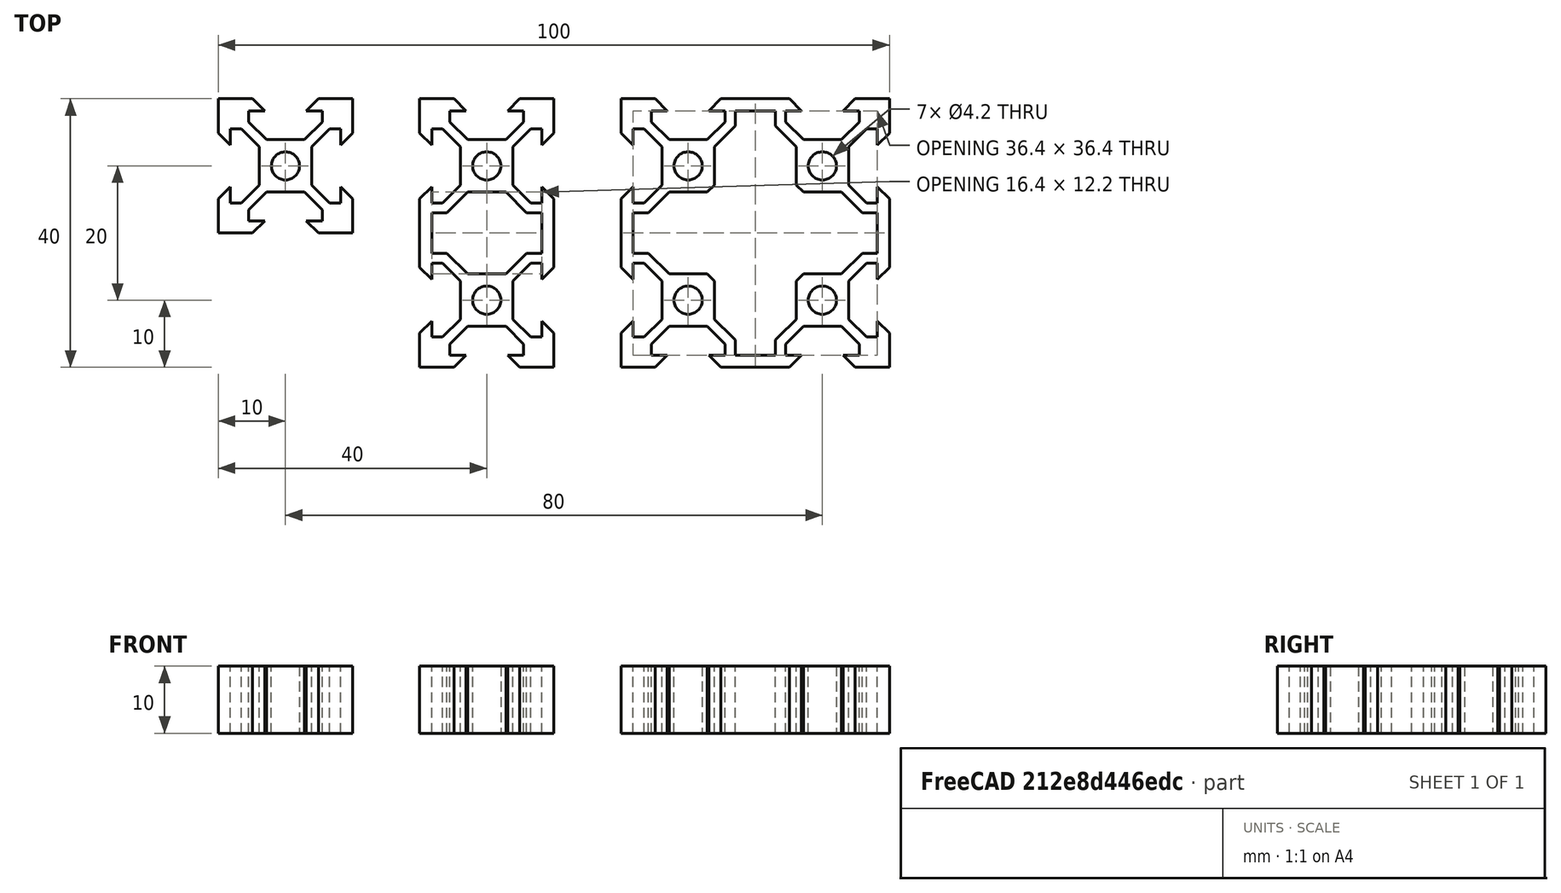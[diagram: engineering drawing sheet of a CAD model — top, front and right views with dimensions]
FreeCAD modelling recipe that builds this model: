
FCSTD DOCUMENT  (FreeCAD 0.19R24291 (Git))
Label: v slot
License: Free for Commercial Use
objects: Sketcher::SketchObject×3, Part::Extrusion×3
note: 6 computed .brp shape members not serialized (recipe doc carries the construction recipe); baked Part::Feature solids carry a one-line shape summary decoded from their .brp

FEATURE [Sketcher::SketchObject] Sketch
  FullyConstrained = false
  sketch-geometry (49):
    g0: Circle CenterX=0 CenterY=0 CenterZ=0 NormalX=0 NormalY=0 NormalZ=-1 AngleXU=0 Radius=2.1
    g1: LineSegment StartX=-2.84 StartY=3.90066 StartZ=0 EndX=-5.49934 EndY=6.56 EndZ=0
    g2: LineSegment StartX=-5.49934 StartY=6.56 StartZ=0 EndX=-5.49934 EndY=8.2 EndZ=0
    g3: LineSegment StartX=-5.49934 StartY=8.2 StartZ=0 EndX=-3.1 EndY=8.2 EndZ=0
    g4: LineSegment StartX=-3.1 StartY=8.2 StartZ=0 EndX=-4.9 EndY=10 EndZ=0
    g5: LineSegment StartX=-4.9 StartY=10 StartZ=0 EndX=-10 EndY=10 EndZ=0
    g6: LineSegment StartX=-10 StartY=10 StartZ=0 EndX=-10 EndY=4.9 EndZ=0
    g7: LineSegment StartX=-10 StartY=4.9 StartZ=0 EndX=-8.2 EndY=3.1 EndZ=0
    g8: LineSegment StartX=-8.2 StartY=3.1 StartZ=0 EndX=-8.2 EndY=5.49934 EndZ=0
    g9: LineSegment StartX=-8.2 StartY=5.49934 StartZ=0 EndX=-6.56 EndY=5.49934 EndZ=0
    g10: LineSegment StartX=-6.56 StartY=5.49934 StartZ=0 EndX=-3.90066 EndY=2.84 EndZ=0
    g11: LineSegment StartX=-3.90066 StartY=2.84 StartZ=0 EndX=-3.90066 EndY=-1.3e-15 EndZ=0
    g12: LineSegment StartX=-3.90066 StartY=-1.1e-15 StartZ=0 EndX=-3.90066 EndY=-2.84 EndZ=0
    g13: LineSegment StartX=-3.90066 StartY=-2.84 StartZ=0 EndX=-6.56 EndY=-5.49934 EndZ=0
    g14: LineSegment StartX=-6.56 StartY=-5.49934 StartZ=0 EndX=-8.2 EndY=-5.49934 EndZ=0
    g15: LineSegment StartX=-8.2 StartY=-5.49934 StartZ=0 EndX=-8.2 EndY=-3.1 EndZ=0
    g16: LineSegment StartX=-8.2 StartY=-3.1 StartZ=0 EndX=-10 EndY=-4.9 EndZ=0
    g17: LineSegment StartX=-10 StartY=-4.9 StartZ=0 EndX=-10 EndY=-10 EndZ=0
    g18: LineSegment StartX=-10 StartY=-10 StartZ=0 EndX=-4.9 EndY=-10 EndZ=0
    g19: LineSegment StartX=-4.9 StartY=-10 StartZ=0 EndX=-3.1 EndY=-8.2 EndZ=0
    g20: LineSegment StartX=-3.1 StartY=-8.2 StartZ=0 EndX=-5.49934 EndY=-8.2 EndZ=0
    g21: LineSegment StartX=-5.49934 StartY=-8.2 StartZ=0 EndX=-5.49934 EndY=-6.56 EndZ=0
    g22: LineSegment StartX=-5.49934 StartY=-6.56 StartZ=0 EndX=-2.84 EndY=-3.90066 EndZ=0
    g23: LineSegment StartX=-2.84 StartY=-3.90066 StartZ=0 EndX=-4e-16 EndY=-3.90066 EndZ=0
    g24: LineSegment StartX=-6e-16 StartY=-3.90066 StartZ=0 EndX=2.84 EndY=-3.90066 EndZ=0
    g25: LineSegment StartX=2.84 StartY=-3.90066 StartZ=0 EndX=5.49934 EndY=-6.56 EndZ=0
    g26: LineSegment StartX=5.49934 StartY=-6.56 StartZ=0 EndX=5.49934 EndY=-8.2 EndZ=0
    g27: LineSegment StartX=5.49934 StartY=-8.2 StartZ=0 EndX=3.1 EndY=-8.2 EndZ=0
    g28: LineSegment StartX=3.1 StartY=-8.2 StartZ=0 EndX=4.9 EndY=-10 EndZ=0
    g29: LineSegment StartX=4.9 StartY=-10 StartZ=0 EndX=10 EndY=-10 EndZ=0
    g30: LineSegment StartX=10 StartY=-10 StartZ=0 EndX=10 EndY=-4.9 EndZ=0
    g31: LineSegment StartX=10 StartY=-4.9 StartZ=0 EndX=8.2 EndY=-3.1 EndZ=0
    g32: LineSegment StartX=8.2 StartY=-3.1 StartZ=0 EndX=8.2 EndY=-5.49934 EndZ=0
    g33: LineSegment StartX=8.2 StartY=-5.49934 StartZ=0 EndX=6.56 EndY=-5.49934 EndZ=0
    g34: LineSegment StartX=6.56 StartY=-5.49934 StartZ=0 EndX=3.90066 EndY=-2.84 EndZ=0
    g35: LineSegment StartX=3.90066 StartY=-2.84 StartZ=0 EndX=3.90066 EndY=-1.3e-15 EndZ=0
    g36: LineSegment StartX=3.90066 StartY=-1.1e-15 StartZ=0 EndX=3.90066 EndY=2.84 EndZ=0
    g37: LineSegment StartX=3.90066 StartY=2.84 StartZ=0 EndX=6.56 EndY=5.49934 EndZ=0
    g38: LineSegment StartX=6.56 StartY=5.49934 StartZ=0 EndX=8.2 EndY=5.49934 EndZ=0
    g39: LineSegment StartX=8.2 StartY=5.49934 StartZ=0 EndX=8.2 EndY=3.1 EndZ=0
    g40: LineSegment StartX=8.2 StartY=3.1 StartZ=0 EndX=10 EndY=4.9 EndZ=0
    g41: LineSegment StartX=10 StartY=4.9 StartZ=0 EndX=10 EndY=10 EndZ=0
    g42: LineSegment StartX=10 StartY=10 StartZ=0 EndX=4.9 EndY=10 EndZ=0
    g43: LineSegment StartX=4.9 StartY=10 StartZ=0 EndX=3.1 EndY=8.2 EndZ=0
    g44: LineSegment StartX=3.1 StartY=8.2 StartZ=0 EndX=5.49934 EndY=8.2 EndZ=0
    g45: LineSegment StartX=5.49934 StartY=8.2 StartZ=0 EndX=5.49934 EndY=6.56 EndZ=0
    g46: LineSegment StartX=5.49934 StartY=6.56 StartZ=0 EndX=2.84 EndY=3.90066 EndZ=0
    g47: LineSegment StartX=2.84 StartY=3.90066 StartZ=0 EndX=0 EndY=3.90066 EndZ=0
    g48: LineSegment StartX=0 StartY=3.90066 StartZ=0 EndX=-2.84 EndY=3.90066 EndZ=0
FEATURE [Part::Extrusion] Extrude  label="2020"
  Base = -> Sketch
  Dir = (0,0,1)
  DirMode = 2
  FaceMakerClass = Part::FaceMakerBullseye
  LengthFwd = 10
  LengthRev = 0
  Solid = true
  Symmetric = false
FEATURE [Sketcher::SketchObject] Sketch001
  FullyConstrained = false
  sketch-geometry (88):
    g0: LineSegment StartX=35.9387 StartY=-6.99934 StartZ=0 EndX=32.84 EndY=-3.90066 EndZ=0
    g1: LineSegment StartX=32.84 StartY=-3.90066 StartZ=0 EndX=30 EndY=-3.90066 EndZ=0
    g2: LineSegment StartX=30 StartY=-3.90066 StartZ=0 EndX=27.16 EndY=-3.90066 EndZ=0
    g3: LineSegment StartX=27.16 StartY=-3.90066 StartZ=0 EndX=24.0613 EndY=-6.99934 EndZ=0
    g4: LineSegment StartX=24.0613 StartY=-6.99934 StartZ=0 EndX=21.8 EndY=-6.99934 EndZ=0
    g5: LineSegment StartX=21.8 StartY=-6.99934 StartZ=0 EndX=21.8 EndY=-13.0007 EndZ=0
    g6: LineSegment StartX=21.8 StartY=-13.0007 StartZ=0 EndX=24.0613 EndY=-13.0007 EndZ=0
    g7: LineSegment StartX=24.0613 StartY=-13.0007 StartZ=0 EndX=27.16 EndY=-16.0993 EndZ=0
    g8: LineSegment StartX=27.16 StartY=-16.0993 StartZ=0 EndX=30 EndY=-16.0993 EndZ=0
    g9: LineSegment StartX=30 StartY=-16.0993 StartZ=0 EndX=32.84 EndY=-16.0993 EndZ=0
    g10: LineSegment StartX=32.84 StartY=-16.0993 StartZ=0 EndX=35.9387 EndY=-13.0007 EndZ=0
    g11: LineSegment StartX=35.9387 StartY=-13.0007 StartZ=0 EndX=38.2 EndY=-13.0007 EndZ=0
    g12: LineSegment StartX=38.2 StartY=-13.0007 StartZ=0 EndX=38.2 EndY=-6.99934 EndZ=0
    g13: LineSegment StartX=38.2 StartY=-6.99934 StartZ=0 EndX=35.9387 EndY=-6.99934 EndZ=0
    g14: LineSegment StartX=20 StartY=10 StartZ=0 EndX=20 EndY=4.9 EndZ=0
    g15: LineSegment StartX=26.0993 StartY=-9e-16 StartZ=0 EndX=26.0993 EndY=-2.84 EndZ=0
    g16: LineSegment StartX=24.5007 StartY=8.2 StartZ=0 EndX=26.9 EndY=8.2 EndZ=0
    g17: LineSegment StartX=24.5007 StartY=8.2 StartZ=0 EndX=24.5007 EndY=6.56 EndZ=0
    g18: LineSegment StartX=25.1 StartY=10 StartZ=0 EndX=20 EndY=10 EndZ=0
    g19: LineSegment StartX=21.8 StartY=-3.1 StartZ=0 EndX=20 EndY=-4.9 EndZ=0
    g20: LineSegment StartX=38.2 StartY=5.49934 StartZ=0 EndX=36.56 EndY=5.49934 EndZ=0
    g21: LineSegment StartX=38.2 StartY=3.1 StartZ=0 EndX=40 EndY=4.9 EndZ=0
    g22: LineSegment StartX=33.9007 StartY=2.84 StartZ=0 EndX=36.56 EndY=5.49934 EndZ=0
    g23: LineSegment StartX=40 StartY=4.9 StartZ=0 EndX=40 EndY=10 EndZ=0
    g24: LineSegment StartX=26.0993 StartY=-2.84 StartZ=0 EndX=23.44 EndY=-5.49934 EndZ=0
    g25: LineSegment StartX=23.44 StartY=5.49934 StartZ=0 EndX=26.0993 EndY=2.84 EndZ=0
    g26: LineSegment StartX=26.9 StartY=8.2 StartZ=0 EndX=25.1 EndY=10 EndZ=0
    g27: LineSegment StartX=24.5007 StartY=6.56 StartZ=0 EndX=27.16 EndY=3.90066 EndZ=0
    g28: LineSegment StartX=21.8 StartY=3.1 StartZ=0 EndX=21.8 EndY=5.49934 EndZ=0
    g29: LineSegment StartX=33.9007 StartY=-2.84 StartZ=0 EndX=36.56 EndY=-5.49934 EndZ=0
    g30: LineSegment StartX=21.8 StartY=-5.49934 StartZ=0 EndX=23.44 EndY=-5.49934 EndZ=0
    g31: LineSegment StartX=21.8 StartY=5.49934 StartZ=0 EndX=23.44 EndY=5.49934 EndZ=0
    g32: LineSegment StartX=35.4993 StartY=8.2 StartZ=0 EndX=35.4993 EndY=6.56 EndZ=0
    g33: LineSegment StartX=33.1 StartY=8.2 StartZ=0 EndX=35.4993 EndY=8.2 EndZ=0
    g34: LineSegment StartX=38.2 StartY=-3.1 StartZ=0 EndX=38.2 EndY=-5.49934 EndZ=0
    g35: LineSegment StartX=38.2 StartY=-5.49934 StartZ=0 EndX=36.56 EndY=-5.49934 EndZ=0
    g36: LineSegment StartX=26.0993 StartY=-9e-16 StartZ=0 EndX=26.0993 EndY=2.84 EndZ=0
    g37: LineSegment StartX=35.4993 StartY=6.56 StartZ=0 EndX=32.84 EndY=3.90066 EndZ=0
    g38: LineSegment StartX=38.2 StartY=5.49934 StartZ=0 EndX=38.2 EndY=3.1 EndZ=0
    g39: Circle CenterX=30 CenterY=0 CenterZ=0 NormalX=0 NormalY=0 NormalZ=-1 AngleXU=0 Radius=2.1
    g40: LineSegment StartX=30 StartY=3.90066 StartZ=0 EndX=32.84 EndY=3.90066 EndZ=0
    g41: LineSegment StartX=33.9007 StartY=-9e-16 StartZ=0 EndX=33.9007 EndY=2.84 EndZ=0
    g42: LineSegment StartX=21.8 StartY=-5.49934 StartZ=0 EndX=21.8 EndY=-3.1 EndZ=0
    g43: LineSegment StartX=40 StartY=-10 StartZ=0 EndX=40 EndY=-4.9 EndZ=0
    g44: LineSegment StartX=30 StartY=3.90066 StartZ=0 EndX=27.16 EndY=3.90066 EndZ=0
    g45: LineSegment StartX=40 StartY=10 StartZ=0 EndX=34.9 EndY=10 EndZ=0
    g46: LineSegment StartX=33.1 StartY=8.2 StartZ=0 EndX=34.9 EndY=10 EndZ=0
    g47: LineSegment StartX=33.9007 StartY=-9e-16 StartZ=0 EndX=33.9007 EndY=-2.84 EndZ=0
    g48: LineSegment StartX=38.2 StartY=-3.1 StartZ=0 EndX=40 EndY=-4.9 EndZ=0
    g49: LineSegment StartX=21.8 StartY=3.1 StartZ=0 EndX=20 EndY=4.9 EndZ=0
    g50: LineSegment StartX=20 StartY=-4.9 StartZ=0 EndX=20 EndY=-10 EndZ=0
    g51: LineSegment StartX=38.2 StartY=-14.5007 StartZ=0 EndX=38.2 EndY=-16.9 EndZ=0
    g52: LineSegment StartX=38.2 StartY=-23.1 StartZ=0 EndX=38.2 EndY=-25.4993 EndZ=0
    g53: LineSegment StartX=33.9007 StartY=-17.16 StartZ=0 EndX=36.56 EndY=-14.5007 EndZ=0
    g54: LineSegment StartX=32.84 StartY=-23.9007 StartZ=0 EndX=35.4993 EndY=-26.56 EndZ=0
    g55: LineSegment StartX=38.2 StartY=-25.4993 StartZ=0 EndX=36.56 EndY=-25.4993 EndZ=0
    g56: LineSegment StartX=33.9007 StartY=-22.84 StartZ=0 EndX=36.56 EndY=-25.4993 EndZ=0
    g57: LineSegment StartX=38.2 StartY=-14.5007 StartZ=0 EndX=36.56 EndY=-14.5007 EndZ=0
    g58: LineSegment StartX=35.4993 StartY=-28.2 StartZ=0 EndX=35.4993 EndY=-26.56 EndZ=0
    g59: LineSegment StartX=34.9 StartY=-30 StartZ=0 EndX=40 EndY=-30 EndZ=0
    g60: LineSegment StartX=33.9007 StartY=-20 StartZ=0 EndX=33.9007 EndY=-17.16 EndZ=0
    g61: LineSegment StartX=38.2 StartY=-16.9 StartZ=0 EndX=40 EndY=-15.1 EndZ=0
    g62: LineSegment StartX=24.5007 StartY=-26.56 StartZ=0 EndX=27.16 EndY=-23.9007 EndZ=0
    g63: LineSegment StartX=21.8 StartY=-14.5007 StartZ=0 EndX=23.44 EndY=-14.5007 EndZ=0
    g64: LineSegment StartX=26.9 StartY=-28.2 StartZ=0 EndX=24.5007 EndY=-28.2 EndZ=0
    g65: LineSegment StartX=26.0993 StartY=-20 StartZ=0 EndX=26.0993 EndY=-17.16 EndZ=0
    g66: LineSegment StartX=30 StartY=-23.9007 StartZ=0 EndX=27.16 EndY=-23.9007 EndZ=0
    g67: LineSegment StartX=21.8 StartY=-16.9 StartZ=0 EndX=21.8 EndY=-14.5007 EndZ=0
    g68: LineSegment StartX=20 StartY=-10 StartZ=0 EndX=20 EndY=-15.1 EndZ=0
    g69: LineSegment StartX=26.0993 StartY=-22.84 StartZ=0 EndX=23.44 EndY=-25.4993 EndZ=0
    g70: LineSegment StartX=21.8 StartY=-16.9 StartZ=0 EndX=20 EndY=-15.1 EndZ=0
    g71: LineSegment StartX=21.8 StartY=-25.4993 StartZ=0 EndX=21.8 EndY=-23.1 EndZ=0
    g72: LineSegment StartX=26.0993 StartY=-20 StartZ=0 EndX=26.0993 EndY=-22.84 EndZ=0
    g73: LineSegment StartX=33.9007 StartY=-20 StartZ=0 EndX=33.9007 EndY=-22.84 EndZ=0
    g74: LineSegment StartX=40 StartY=-30 StartZ=0 EndX=40 EndY=-24.9 EndZ=0
    g75: LineSegment StartX=26.9 StartY=-28.2 StartZ=0 EndX=25.1 EndY=-30 EndZ=0
    g76: LineSegment StartX=24.5007 StartY=-28.2 StartZ=0 EndX=24.5007 EndY=-26.56 EndZ=0
    g77: LineSegment StartX=21.8 StartY=-23.1 StartZ=0 EndX=20 EndY=-24.9 EndZ=0
    g78: LineSegment StartX=23.44 StartY=-14.5007 StartZ=0 EndX=26.0993 EndY=-17.16 EndZ=0
    g79: LineSegment StartX=21.8 StartY=-25.4993 StartZ=0 EndX=23.44 EndY=-25.4993 EndZ=0
    g80: LineSegment StartX=20 StartY=-24.9 StartZ=0 EndX=20 EndY=-30 EndZ=0
    g81: LineSegment StartX=20 StartY=-30 StartZ=0 EndX=25.1 EndY=-30 EndZ=0
    g82: Circle CenterX=30 CenterY=-20 CenterZ=0 NormalX=0 NormalY=0 NormalZ=-1 AngleXU=0 Radius=2.1
    g83: LineSegment StartX=38.2 StartY=-23.1 StartZ=0 EndX=40 EndY=-24.9 EndZ=0
    g84: LineSegment StartX=35.4993 StartY=-28.2 StartZ=0 EndX=33.1 EndY=-28.2 EndZ=0
    g85: LineSegment StartX=40 StartY=-15.1 StartZ=0 EndX=40 EndY=-10 EndZ=0
    g86: LineSegment StartX=33.1 StartY=-28.2 StartZ=0 EndX=34.9 EndY=-30 EndZ=0
    g87: LineSegment StartX=30 StartY=-23.9007 StartZ=0 EndX=32.84 EndY=-23.9007 EndZ=0
FEATURE [Sketcher::SketchObject] Sketch002
  FullyConstrained = false
  sketch-geometry (144):
    g0: LineSegment StartX=51.8 StartY=-5.49934 StartZ=0 EndX=51.8 EndY=-3.1 EndZ=0
    g1: LineSegment StartX=51.8 StartY=-16.9 StartZ=0 EndX=50 EndY=-15.1 EndZ=0
    g2: LineSegment StartX=51.8 StartY=-23.1 StartZ=0 EndX=50 EndY=-24.9 EndZ=0
    g3: LineSegment StartX=50 StartY=-30 StartZ=0 EndX=55.1 EndY=-30 EndZ=0
    g4: LineSegment StartX=51.8 StartY=-3.1 StartZ=0 EndX=50 EndY=-4.9 EndZ=0
    g5: LineSegment StartX=51.8 StartY=-6.99934 StartZ=0 EndX=51.8 EndY=-13.0007 EndZ=0
    g6: LineSegment StartX=56.0993 StartY=-20 StartZ=0 EndX=56.0993 EndY=-17.16 EndZ=0
    g7: LineSegment StartX=60 StartY=-16.0993 StartZ=0 EndX=57.16 EndY=-16.0993 EndZ=0
    g8: LineSegment StartX=56.0993 StartY=-20 StartZ=0 EndX=56.0993 EndY=-22.84 EndZ=0
    g9: LineSegment StartX=50 StartY=-10 StartZ=0 EndX=50 EndY=-15.1 EndZ=0
    g10: LineSegment StartX=51.8 StartY=-14.5007 StartZ=0 EndX=53.44 EndY=-14.5007 EndZ=0
    g11: LineSegment StartX=51.8 StartY=-25.4993 StartZ=0 EndX=53.44 EndY=-25.4993 EndZ=0
    g12: LineSegment StartX=56.9 StartY=-28.2 StartZ=0 EndX=54.5007 EndY=-28.2 EndZ=0
    g13: LineSegment StartX=54.5007 StartY=-28.2 StartZ=0 EndX=54.5007 EndY=-26.56 EndZ=0
    g14: LineSegment StartX=56.0993 StartY=-22.84 StartZ=0 EndX=53.44 EndY=-25.4993 EndZ=0
    g15: LineSegment StartX=51.8 StartY=-6.99934 StartZ=0 EndX=54.0613 EndY=-6.99934 EndZ=0
    g16: LineSegment StartX=50 StartY=-24.9 StartZ=0 EndX=50 EndY=-30 EndZ=0
    g17: LineSegment StartX=51.8 StartY=-5.49934 StartZ=0 EndX=53.44 EndY=-5.49934 EndZ=0
    g18: LineSegment StartX=56.0993 StartY=-2.84 StartZ=0 EndX=53.44 EndY=-5.49934 EndZ=0
    g19: LineSegment StartX=50 StartY=-4.9 StartZ=0 EndX=50 EndY=-10 EndZ=0
    g20: LineSegment StartX=54.0613 StartY=-6.99934 StartZ=0 EndX=57.16 EndY=-3.90066 EndZ=0
    g21: LineSegment StartX=50 StartY=10 StartZ=0 EndX=50 EndY=4.9 EndZ=0
    g22: LineSegment StartX=53.44 StartY=5.49934 StartZ=0 EndX=56.0993 EndY=2.84 EndZ=0
    g23: LineSegment StartX=55.1 StartY=10 StartZ=0 EndX=50 EndY=10 EndZ=0
    g24: LineSegment StartX=51.8 StartY=3.1 StartZ=0 EndX=51.8 EndY=5.49934 EndZ=0
    g25: LineSegment StartX=56.9 StartY=-28.2 StartZ=0 EndX=55.1 EndY=-30 EndZ=0
    g26: LineSegment StartX=54.0613 StartY=-13.0007 StartZ=0 EndX=57.16 EndY=-16.0993 EndZ=0
    g27: LineSegment StartX=54.5007 StartY=-26.56 StartZ=0 EndX=57.16 EndY=-23.9007 EndZ=0
    g28: LineSegment StartX=56.0993 StartY=-9e-16 StartZ=0 EndX=56.0993 EndY=-2.84 EndZ=0
    g29: LineSegment StartX=51.8 StartY=-16.9 StartZ=0 EndX=51.8 EndY=-14.5007 EndZ=0
    g30: LineSegment StartX=51.8 StartY=-25.4993 StartZ=0 EndX=51.8 EndY=-23.1 EndZ=0
    g31: LineSegment StartX=53.44 StartY=-14.5007 StartZ=0 EndX=56.0993 EndY=-17.16 EndZ=0
    g32: LineSegment StartX=51.8 StartY=-13.0007 StartZ=0 EndX=54.0613 EndY=-13.0007 EndZ=0
    g33: LineSegment StartX=56.0993 StartY=-9e-16 StartZ=0 EndX=56.0993 EndY=2.84 EndZ=0
    g34: LineSegment StartX=54.5007 StartY=6.56 StartZ=0 EndX=57.16 EndY=3.90066 EndZ=0
    g35: LineSegment StartX=51.8 StartY=3.1 StartZ=0 EndX=50 EndY=4.9 EndZ=0
    g36: LineSegment StartX=54.5007 StartY=8.2 StartZ=0 EndX=56.9 EndY=8.2 EndZ=0
    g37: LineSegment StartX=51.8 StartY=5.49934 StartZ=0 EndX=53.44 EndY=5.49934 EndZ=0
    g38: LineSegment StartX=54.5007 StartY=8.2 StartZ=0 EndX=54.5007 EndY=6.56 EndZ=0
    g39: LineSegment StartX=56.9 StartY=8.2 StartZ=0 EndX=55.1 EndY=10 EndZ=0
    g40: Circle CenterX=60 CenterY=-20 CenterZ=0 NormalX=0 NormalY=0 NormalZ=-1 AngleXU=0 Radius=2.1
    g41: LineSegment StartX=63.9007 StartY=-22.84 StartZ=0 EndX=66.56 EndY=-25.4993 EndZ=0
    g42: LineSegment StartX=60 StartY=-23.9007 StartZ=0 EndX=62.84 EndY=-23.9007 EndZ=0
    g43: LineSegment StartX=63.9007 StartY=-20 StartZ=0 EndX=63.9007 EndY=-17.16 EndZ=0
    g44: LineSegment StartX=63.1 StartY=-28.2 StartZ=0 EndX=64.9 EndY=-30 EndZ=0
    g45: LineSegment StartX=63.9007 StartY=-20 StartZ=0 EndX=63.9007 EndY=-22.84 EndZ=0
    g46: LineSegment StartX=64.9 StartY=-30 StartZ=0 EndX=70 EndY=-30 EndZ=0
    g47: LineSegment StartX=60 StartY=-23.9007 StartZ=0 EndX=57.16 EndY=-23.9007 EndZ=0
    g48: LineSegment StartX=60 StartY=3.90066 StartZ=0 EndX=57.16 EndY=3.90066 EndZ=0
    g49: LineSegment StartX=63.9007 StartY=-9e-16 StartZ=0 EndX=63.9007 EndY=-2.84 EndZ=0
    g50: LineSegment StartX=60 StartY=-3.90066 StartZ=0 EndX=57.16 EndY=-3.90066 EndZ=0
    g51: LineSegment StartX=65.4993 StartY=8.2 StartZ=0 EndX=65.4993 EndY=6.56 EndZ=0
    g52: LineSegment StartX=70 StartY=10 StartZ=0 EndX=64.9 EndY=10 EndZ=0
    g53: LineSegment StartX=63.9007 StartY=2.84 StartZ=0 EndX=66.56 EndY=5.49934 EndZ=0
    g54: LineSegment StartX=65.4993 StartY=6.56 StartZ=0 EndX=62.84 EndY=3.90066 EndZ=0
    g55: LineSegment StartX=60 StartY=-16.0993 StartZ=0 EndX=62.84 EndY=-16.0993 EndZ=0
    g56: LineSegment StartX=63.9007 StartY=-9e-16 StartZ=0 EndX=63.9007 EndY=2.84 EndZ=0
    g57: LineSegment StartX=63.1 StartY=8.2 StartZ=0 EndX=64.9 EndY=10 EndZ=0
    g58: LineSegment StartX=65.4993 StartY=-28.2 StartZ=0 EndX=63.1 EndY=-28.2 EndZ=0
    g59: LineSegment StartX=65.4993 StartY=-28.2 StartZ=0 EndX=65.4993 EndY=-26.56 EndZ=0
    g60: LineSegment StartX=60 StartY=-3.90066 StartZ=0 EndX=62.84 EndY=-3.90066 EndZ=0
    g61: LineSegment StartX=60 StartY=3.90066 StartZ=0 EndX=62.84 EndY=3.90066 EndZ=0
    g62: Circle CenterX=60 CenterY=0 CenterZ=0 NormalX=0 NormalY=0 NormalZ=-1 AngleXU=0 Radius=2.1
    g63: LineSegment StartX=63.1 StartY=8.2 StartZ=0 EndX=65.4993 EndY=8.2 EndZ=0
    g64: LineSegment StartX=62.84 StartY=-23.9007 StartZ=0 EndX=65.4993 EndY=-26.56 EndZ=0
    g65: LineSegment StartX=85.4993 StartY=8.2 StartZ=0 EndX=85.4993 EndY=6.56 EndZ=0
    g66: LineSegment StartX=83.9007 StartY=-17.16 StartZ=0 EndX=86.56 EndY=-14.5007 EndZ=0
    g67: LineSegment StartX=76.0993 StartY=-9e-16 StartZ=0 EndX=76.0993 EndY=2.84 EndZ=0
    g68: LineSegment StartX=88.2 StartY=5.49934 StartZ=0 EndX=86.56 EndY=5.49934 EndZ=0
    g69: LineSegment StartX=85.9387 StartY=-13.0007 StartZ=0 EndX=88.2 EndY=-13.0007 EndZ=0
    g70: LineSegment StartX=88.2 StartY=5.49934 StartZ=0 EndX=88.2 EndY=3.1 EndZ=0
    g71: LineSegment StartX=83.9007 StartY=-9e-16 StartZ=0 EndX=83.9007 EndY=2.84 EndZ=0
    g72: LineSegment StartX=83.1 StartY=8.2 StartZ=0 EndX=85.4993 EndY=8.2 EndZ=0
    g73: LineSegment StartX=73.44 StartY=5.49934 StartZ=0 EndX=76.0993 EndY=2.84 EndZ=0
    g74: LineSegment StartX=90 StartY=-30 StartZ=0 EndX=90 EndY=-24.9 EndZ=0
    g75: LineSegment StartX=76.0993 StartY=-20 StartZ=0 EndX=76.0993 EndY=-22.84 EndZ=0
    g76: Circle CenterX=80 CenterY=-20 CenterZ=0 NormalX=0 NormalY=0 NormalZ=-1 AngleXU=0 Radius=2.1
    g77: LineSegment StartX=85.4993 StartY=-28.2 StartZ=0 EndX=83.1 EndY=-28.2 EndZ=0
    g78: LineSegment StartX=80 StartY=-23.9007 StartZ=0 EndX=77.16 EndY=-23.9007 EndZ=0
    g79: LineSegment StartX=85.4993 StartY=-28.2 StartZ=0 EndX=85.4993 EndY=-26.56 EndZ=0
    g80: LineSegment StartX=76.0993 StartY=-22.84 StartZ=0 EndX=73.44 EndY=-25.4993 EndZ=0
    g81: LineSegment StartX=82.84 StartY=-23.9007 StartZ=0 EndX=85.4993 EndY=-26.56 EndZ=0
    g82: LineSegment StartX=88.2 StartY=-25.4993 StartZ=0 EndX=86.56 EndY=-25.4993 EndZ=0
    g83: LineSegment StartX=83.1 StartY=-28.2 StartZ=0 EndX=84.9 EndY=-30 EndZ=0
    g84: LineSegment StartX=80 StartY=-23.9007 StartZ=0 EndX=82.84 EndY=-23.9007 EndZ=0
    g85: LineSegment StartX=88.2 StartY=-6.99934 StartZ=0 EndX=88.2 EndY=-13.0007 EndZ=0
    g86: LineSegment StartX=83.9007 StartY=-9e-16 StartZ=0 EndX=83.9007 EndY=-2.84 EndZ=0
    g87: LineSegment StartX=76.0993 StartY=-9e-16 StartZ=0 EndX=76.0993 EndY=-2.84 EndZ=0
    g88: LineSegment StartX=88.2 StartY=-5.49934 StartZ=0 EndX=86.56 EndY=-5.49934 EndZ=0
    g89: LineSegment StartX=88.2 StartY=-14.5007 StartZ=0 EndX=88.2 EndY=-16.9 EndZ=0
    g90: LineSegment StartX=90 StartY=-15.1 StartZ=0 EndX=90 EndY=-10 EndZ=0
    g91: LineSegment StartX=88.2 StartY=-16.9 StartZ=0 EndX=90 EndY=-15.1 EndZ=0
    g92: LineSegment StartX=80 StartY=3.90066 StartZ=0 EndX=77.16 EndY=3.90066 EndZ=0
    g93: LineSegment StartX=80 StartY=-16.0993 StartZ=0 EndX=77.16 EndY=-16.0993 EndZ=0
    g94: LineSegment StartX=90 StartY=-10 StartZ=0 EndX=90 EndY=-4.9 EndZ=0
    g95: LineSegment StartX=75.1 StartY=10 StartZ=0 EndX=70 EndY=10 EndZ=0
    g96: LineSegment StartX=88.2 StartY=-3.1 StartZ=0 EndX=88.2 EndY=-5.49934 EndZ=0
    g97: LineSegment StartX=74.5007 StartY=6.56 StartZ=0 EndX=77.16 EndY=3.90066 EndZ=0
    g98: LineSegment StartX=90 StartY=4.9 StartZ=0 EndX=90 EndY=10 EndZ=0
    g99: LineSegment StartX=80 StartY=-3.90066 StartZ=0 EndX=82.84 EndY=-3.90066 EndZ=0
    g100: LineSegment StartX=80 StartY=-16.0993 StartZ=0 EndX=82.84 EndY=-16.0993 EndZ=0
    g101: LineSegment StartX=85.9387 StartY=-13.0007 StartZ=0 EndX=82.84 EndY=-16.0993 EndZ=0
    g102: LineSegment StartX=82.84 StartY=-3.90066 StartZ=0 EndX=85.9387 EndY=-6.99934 EndZ=0
    g103: LineSegment StartX=83.9007 StartY=-2.84 StartZ=0 EndX=86.56 EndY=-5.49934 EndZ=0
    g104: LineSegment StartX=88.2 StartY=-3.1 StartZ=0 EndX=90 EndY=-4.9 EndZ=0
    g105: LineSegment StartX=80 StartY=3.90066 StartZ=0 EndX=82.84 EndY=3.90066 EndZ=0
    g106: Circle CenterX=80 CenterY=0 CenterZ=0 NormalX=0 NormalY=0 NormalZ=-1 AngleXU=0 Radius=2.1
    g107: LineSegment StartX=83.1 StartY=8.2 StartZ=0 EndX=84.9 EndY=10 EndZ=0
    g108: LineSegment StartX=85.4993 StartY=6.56 StartZ=0 EndX=82.84 EndY=3.90066 EndZ=0
    g109: LineSegment StartX=76.9 StartY=8.2 StartZ=0 EndX=75.1 EndY=10 EndZ=0
    g110: LineSegment StartX=74.5007 StartY=8.2 StartZ=0 EndX=74.5007 EndY=6.56 EndZ=0
    g111: LineSegment StartX=90 StartY=10 StartZ=0 EndX=84.9 EndY=10 EndZ=0
    g112: LineSegment StartX=85.9387 StartY=-6.99934 StartZ=0 EndX=88.2 EndY=-6.99934 EndZ=0
    g113: LineSegment StartX=88.2 StartY=3.1 StartZ=0 EndX=90 EndY=4.9 EndZ=0
    g114: LineSegment StartX=83.9007 StartY=2.84 StartZ=0 EndX=86.56 EndY=5.49934 EndZ=0
    g115: LineSegment StartX=88.2 StartY=-14.5007 StartZ=0 EndX=86.56 EndY=-14.5007 EndZ=0
    g116: LineSegment StartX=74.5007 StartY=8.2 StartZ=0 EndX=76.9 EndY=8.2 EndZ=0
    g117: LineSegment StartX=80 StartY=-3.90066 StartZ=0 EndX=77.16 EndY=-3.90066 EndZ=0
    g118: LineSegment StartX=74.5007 StartY=-26.56 StartZ=0 EndX=77.16 EndY=-23.9007 EndZ=0
    g119: LineSegment StartX=76.9 StartY=-28.2 StartZ=0 EndX=74.5007 EndY=-28.2 EndZ=0
    g120: LineSegment StartX=76.9 StartY=-28.2 StartZ=0 EndX=75.1 EndY=-30 EndZ=0
    g121: LineSegment StartX=84.9 StartY=-30 StartZ=0 EndX=90 EndY=-30 EndZ=0
    g122: LineSegment StartX=88.2 StartY=-23.1 StartZ=0 EndX=90 EndY=-24.9 EndZ=0
    g123: LineSegment StartX=76.0993 StartY=-20 StartZ=0 EndX=76.0993 EndY=-17.16 EndZ=0
    g124: LineSegment StartX=70 StartY=-30 StartZ=0 EndX=75.1 EndY=-30 EndZ=0
    g125: LineSegment StartX=83.9007 StartY=-20 StartZ=0 EndX=83.9007 EndY=-17.16 EndZ=0
    g126: LineSegment StartX=88.2 StartY=-23.1 StartZ=0 EndX=88.2 EndY=-25.4993 EndZ=0
    g127: LineSegment StartX=74.5007 StartY=-28.2 StartZ=0 EndX=74.5007 EndY=-26.56 EndZ=0
    g128: LineSegment StartX=83.9007 StartY=-22.84 StartZ=0 EndX=86.56 EndY=-25.4993 EndZ=0
    g129: LineSegment StartX=83.9007 StartY=-20 StartZ=0 EndX=83.9007 EndY=-22.84 EndZ=0
    g130: LineSegment StartX=63.9007 StartY=-2.84 StartZ=0 EndX=62.84 EndY=-3.90066 EndZ=0
    g131: LineSegment StartX=76.0993 StartY=-2.84 StartZ=0 EndX=77.16 EndY=-3.90066 EndZ=0
    g132: LineSegment StartX=77.16 StartY=-16.0993 StartZ=0 EndX=76.0993 EndY=-17.16 EndZ=0
    g133: LineSegment StartX=62.84 StartY=-16.0993 StartZ=0 EndX=63.9007 EndY=-17.16 EndZ=0
    g134: LineSegment StartX=66.9993 StartY=8.2 StartZ=0 EndX=73.0007 EndY=8.2 EndZ=0
    g135: LineSegment StartX=66.9993 StartY=8.2 StartZ=0 EndX=66.9993 EndY=5.93868 EndZ=0
    g136: LineSegment StartX=66.56 StartY=5.49934 StartZ=0 EndX=66.9993 EndY=5.93868 EndZ=0
    g137: LineSegment StartX=73.0007 StartY=8.2 StartZ=0 EndX=73.0007 EndY=5.93868 EndZ=0
    g138: LineSegment StartX=73.0007 StartY=5.93868 StartZ=0 EndX=73.44 EndY=5.49934 EndZ=0
    g139: LineSegment StartX=66.9993 StartY=-28.2 StartZ=0 EndX=73.0007 EndY=-28.2 EndZ=0
    g140: LineSegment StartX=66.9993 StartY=-28.2 StartZ=0 EndX=66.9993 EndY=-25.9387 EndZ=0
    g141: LineSegment StartX=66.9993 StartY=-25.9387 StartZ=0 EndX=66.56 EndY=-25.4993 EndZ=0
    g142: LineSegment StartX=73.0007 StartY=-28.2 StartZ=0 EndX=73.0007 EndY=-25.9387 EndZ=0
    g143: LineSegment StartX=73.0007 StartY=-25.9387 StartZ=0 EndX=73.44 EndY=-25.4993 EndZ=0
FEATURE [Part::Extrusion] Extrude001  label="2040"
  Base = -> Sketch001
  Dir = (0,0,1)
  DirMode = 2
  FaceMakerClass = Part::FaceMakerBullseye
  LengthFwd = 10
  LengthRev = 0
  Solid = true
  Symmetric = false
FEATURE [Part::Extrusion] Extrude002  label="4040"
  Base = -> Sketch002
  Dir = (0,0,1)
  DirMode = 2
  FaceMakerClass = Part::FaceMakerBullseye
  LengthFwd = 10
  LengthRev = 0
  Solid = true
  Symmetric = false
